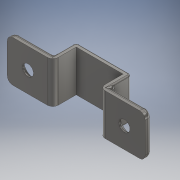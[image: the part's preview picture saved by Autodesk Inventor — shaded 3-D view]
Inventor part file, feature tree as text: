
AUTODESK INVENTOR PART (.ipt)
format: ipt  version: 2018 (Build 220112000, 112)  size: 247,808 bytes
history: native  units: mm
features: fillet x5, sketch x2, extrude x1, hole x1
ambient origin geometry x8: Origin, YZ Plane, XZ Plane, XY Plane, X Axis, Y Axis, Z Axis, Center Point
bodies: Solid1 (feature_tree)
feature tree (9):
  extrude  "Extrusion1"  Depth=16.5mm
  hole  "Hole1"  [1 undecoded]
  fillet  "Fillet5"  Radius=8.5mm
  fillet  "Fillet6"  Radius=15.0mm
  fillet  "Fillet7"  Radius=15.0mm
  fillet  "Fillet8"  Radius=2.5mm
  fillet  "Fillet9"  Radius=7.5mm
  sketch  "Sketch1"  dims[d0=50.0mm d1=16.5mm]
  sketch  "Sketch2"  dims[d2=16.5mm d3=2.5mm d4=8.5mm d5=15.0mm d6=15.0mm d7=2.5mm d8=7.5mm d9=7.5mm d10=15.0mm d11=0.0mm d12=7.5mm d13=7.5mm d14=4.0mm d15=6.0mm d16=8.0mm d17=2.0mm d18=90.0deg d19=8.0mm d20=20.594885mm d25=0.5mm d26=1.0mm d27=1.5mm d28=2.0mm d29=1.5mm]
note: 1 required parameter value undecoded (feature->parameter linkage not recoverable at this tier; creation-order binding heuristic only, values carry confidence <= 0.55)
